# Revit family: CENTUM Festpunkt Typ A m XL100 Massivanschluss, Gummi
name_source: partatom
category: HLS-Bauteile
revit_build: Autodesk Revit 2017 (Build: 20190507_1515(x64)
units: mm (PartAtom-declared; Revit-internal decimal feet)

## family parameters
Arbeitsebenenbasiert = Ja
Beim Laden mit Abzugskörper schneiden = Nein
Bemaßung runder Anschluss = Durchmesser verwenden
Gemeinsam genutzt = Ja
Immer vertikal = Nein
Raumberechnungspunkt = Nein
Teiletyp = Normal

## types (3) — shared parameters
Anzahl Rohrschellen = 2
Aufbaumaß = 79 mm
Ausführung = CENTUM Massivanschluss
Breite Material Rohrschelle = 50 mm
Breite Profilstahl = 120 mm
Fabrikat = MEFA
Firma = MEFA Befestigungs- und Montagesysteme GmbH
Höhe Profilstahl = 55 mm
Kurztext1 = Festpunkt Typ A
Länge Druckstück = 116 mm
Länge Profilstahl = 330 mm  [stored 1.08268 ft]
Material Druckstücke = Stahl
Material Schalldämmeinlage = TPE/EPDM
Materialname Druckstücke = S235JR
Mengeneinheit = St
Oberfläche Druckstücke = blank
Oberfläche Träger + Schellen = galvanisch verzinkt
Profilstahltyp = U120
Rohrschellentyp = Titan HD
Schalldämmeinlage = Gummi
Stärke Material Rohrschelle = 5 mm
Vorgabe-Ansicht = 1219 mm
max. Temperaturbeständigkeit = 100 °C
vpe = 1 St
zero-valued in all types: max. Höhe

## per-type parameters (varying)
| type | Artikelnummer | Breite | EAN | Gewicht | Gewicht pro Bauteil | Kurztext2 | RA | Rohraußendurchmesser | Rohrschelle | max. Axiale Reaktionskraft | max. Rohraußendurchmesser | min. Rohraußendurchmesser |
| CENTUM Festpunkt Typ A, Ø 168,3, m. XL100 Massivanschluss, Gummi | 9993734 | 258 mm  [stored 0.846457 ft] | 4250928454225 | 11.75 kg | 11.75 kg | 168,3 mm Gummi CENTUM Massivanschl. | 132 mm | 168 mm  [stored 0.551181 ft] | MEFA RS Titan HD, Ø168,3-Ø356 mm, TPE : MEFA RS Titan HD, Ø168,3 mm, TPE |  | 0 mm  [stored 0 ft] | 0 mm  [stored 0 ft] |
| CENTUM Festpunkt Typ A, Ø 219,1, m. XL100 Massivanschluss, Gummi | 9992830 | 309 mm  [stored 1.01378 ft] | 4250928454171 | 12.51 kg | 12.51 kg | 219,1 mm Gummi CENTUM Massivanschl. | 161 mm  [stored 0.528215 ft] | 219 mm  [stored 0.718504 ft] | MEFA RS Titan HD, Ø168,3-Ø356 mm, TPE : MEFA RS Titan HD, Ø219 mm, TPE |  | 0 mm  [stored 0 ft] | 0 mm  [stored 0 ft] |
| CENTUM Festpunkt Typ A, Ø 273-274, m. XL100 Massivanschluss, Gummi | 9992178 | 363 mm  [stored 1.19094 ft] | 4250928454164 | 13.32 kg | 13.32 kg | 273 - 274 mm Gummi CENTUM Massivanschl. | 192 mm | 0 mm  [stored 0 ft] | MEFA RS Titan HD, Ø168,3-Ø356 mm, TPE : MEFA RS Titan HD, Ø273-Ø274  mm, TPE | 20 kN | 274 mm  [stored 0.89895 ft] | 273 mm  [stored 0.895669 ft] |

note: [stored X ft] marks values corroborated as IEEE doubles in the binary element streams (Revit-internal decimal feet)

## geometry (parser evidence)
native form markers: Sweep x5
no freeform markers — native parametric forms only
